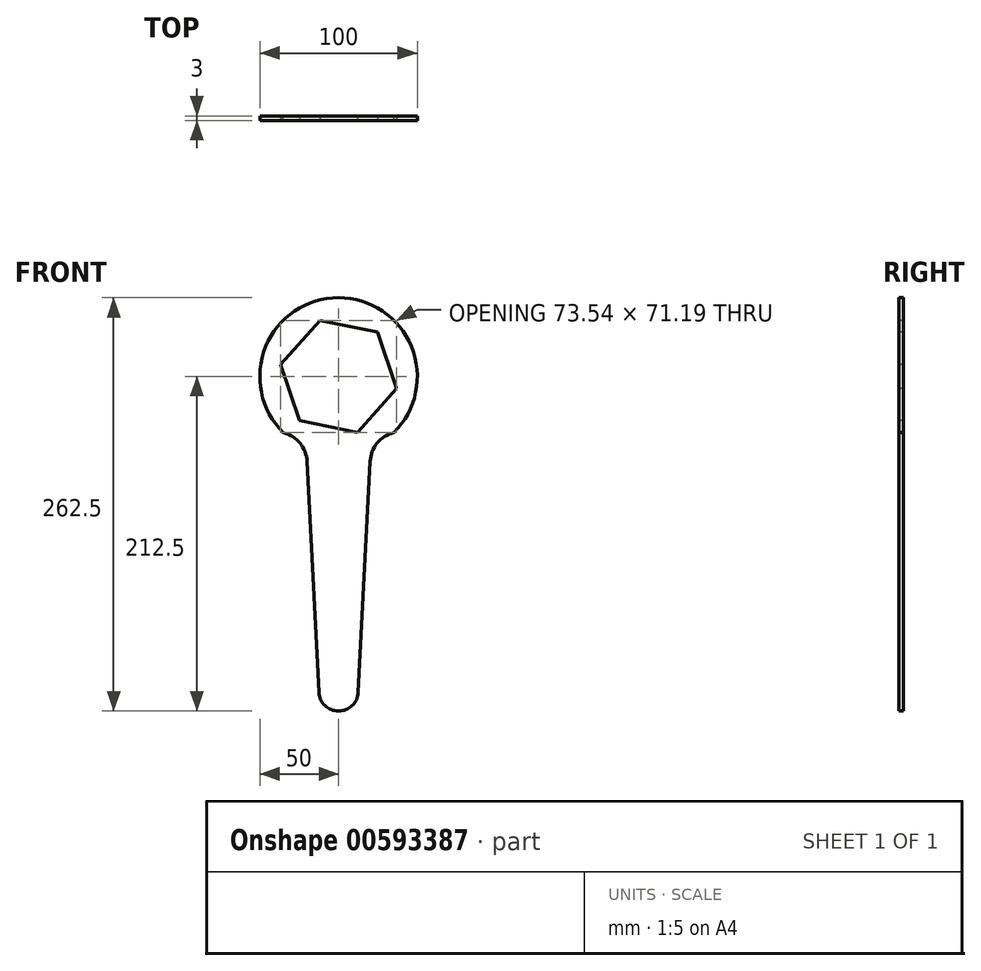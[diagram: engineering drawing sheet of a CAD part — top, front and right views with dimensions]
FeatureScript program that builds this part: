
annotation { "Feature Type Name" : "Feature", "Feature Type Description" : "" }
export const myFeature = defineFeature(function(context is Context, id is Id, definition is map)
    precondition{}
    {
        {
            var Q0;
            Q0=qCreatedBy(makeId("Front.planeOp"),FACE);
            var sketch = newSketch(context, id + "F0", { "sketchPlane" : qUnion([Q0])});
            skCircle(sketch, "E0", {"center": v(0, 0) * mm, "radius": 50 * mm});
            skSolve(sketch);
        }
        {
            var Q0;
            Q0=qCreatedBy(makeId("Front.planeOp"),FACE);
            var sketch = newSketch(context, id + "F1", { "sketchPlane" : qUnion([Q0])});
            skPoint(sketch, "E1", {"position": v(0, -200) * mm});
            skPoint(sketch, "E2", {"position": v(40, -55) * mm});
            skPoint(sketch, "E3", {"position": v(-40, -55) * mm});
            skArc(sketch, "E4", {"start": v(-20.03, -53.97) * mm, "mid": v(-24.54, -42.31) * mm, "end": v(-35.1, -35.6) * mm});
            skArc(sketch, "E5", {"start": v(35.1, -35.6) * mm, "mid": v(24.54, -42.31) * mm, "end": v(20.03, -53.97) * mm});
            skArc(sketch, "E6", {"start": v(-12.48, -200.64) * mm, "mid": v(0, -212.5) * mm, "end": v(12.48, -200.64) * mm});
            skLineSegment(sketch, "E7", {"start": v(-12.48, -200.64) * mm, "end": v(-20.03, -53.97) * mm});
            skLineSegment(sketch, "E8", {"start": v(20.03, -53.97) * mm, "end": v(12.48, -200.64) * mm});
            skArc(sketch, "E9.trimOffspring", {"start": v(35.1, -35.6) * mm, "mid": v(0, 50) * mm, "end": v(-35.1, -35.6) * mm});
            skSolve(sketch);
        }
        {
            var Q0;
            Q0=makeQuery(id+"F1.imprint","IMPRINT",FACE,{"disambiguationData":[TD([[makeQuery(id+"F1.imprint","IMPRINT",EDGE,{"derivedFrom":sQuery(id+"F1.wireOp",EDGE,"E4")}),-1.0]])]});
            extrude(context, id + "F2", {"entities" : qUnion([Q0]), "depth" : 3 * mm});
        }
        {
            var Q0;
            Q0=makeQuery(id+"F2.opExtrude","CAP_FACE",FACE,{"disambiguationData":[OSD([sQuery(id+"F1.wireOp",EDGE,"E4"),sQuery(id+"F1.wireOp",EDGE,"E5"),sQuery(id+"F1.wireOp",EDGE,"E6"),sQuery(id+"F1.wireOp",EDGE,"E7"),sQuery(id+"F1.wireOp",EDGE,"E8"),sQuery(id+"F1.wireOp",EDGE,"E9.trimOffspring")])],"isStart":false});
            var sketch = newSketch(context, id + "F3", { "sketchPlane" : qUnion([Q0])});
            skCircle(sketch, "E10.cCircle", {"center": v(0, 0) * mm, "radius": 32.5 * mm, "construction": true});
            skLineSegment(sketch, "E10.0", {"start": v(11.9, -35.6) * mm, "end": v(-24.88, -28.1) * mm});
            skLineSegment(sketch, "E10.1", {"start": v(-24.88, -28.1) * mm, "end": v(-36.77, 7.5) * mm});
            skLineSegment(sketch, "E10.2", {"start": v(-36.77, 7.5) * mm, "end": v(-11.9, 35.6) * mm});
            skLineSegment(sketch, "E10.3", {"start": v(-11.9, 35.6) * mm, "end": v(24.88, 28.1) * mm});
            skLineSegment(sketch, "E10.4", {"start": v(24.88, 28.1) * mm, "end": v(36.77, -7.5) * mm});
            skLineSegment(sketch, "E10.5", {"start": v(36.77, -7.5) * mm, "end": v(11.9, -35.6) * mm});
            skPoint(sketch, "E10.0.midPoint", {"position": v(-6.5, -31.85) * mm});
            skSolve(sketch);
        }
        {
            var Q0;
            Q0=makeQuery(id+"F3.imprint","IMPRINT",FACE,{"disambiguationData":[TD([[makeQuery(id+"F3.imprint","IMPRINT",EDGE,{"derivedFrom":sQuery(id+"F3.wireOp",EDGE,"E10.0")}),-1.0]])]});
            extrude(context, id + "F4", {"entities" : qUnion([Q0]), "operationType" : NewBodyOperationType.REMOVE, "oppositeDirection" : true, "depth" : 25 * mm});
        }
    });
